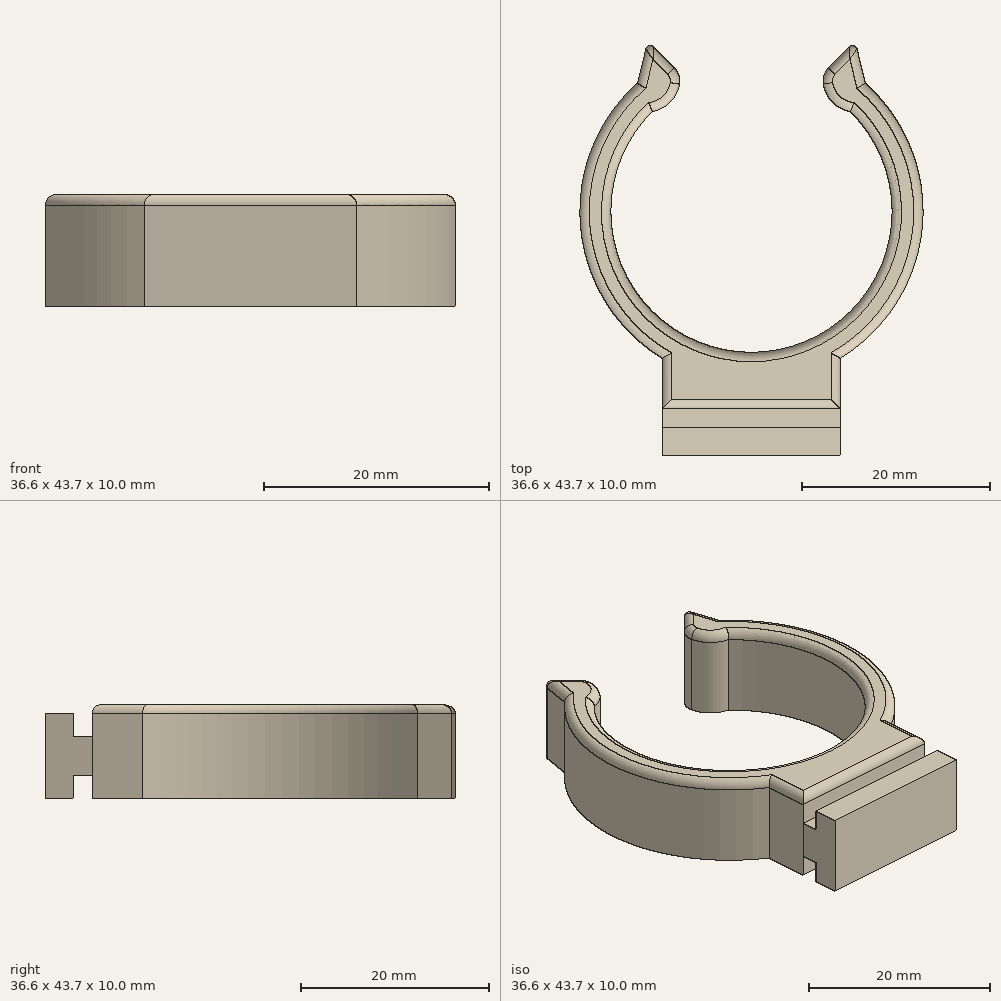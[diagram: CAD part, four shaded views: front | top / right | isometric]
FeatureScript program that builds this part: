
annotation { "Feature Type Name" : "Feature", "Feature Type Description" : "" }
export const myFeature = defineFeature(function(context is Context, id is Id, definition is map)
    precondition{}
    {
        {
            var Q0;
            Q0=qCreatedBy(makeId("Front.planeOp"),FACE);
            var sketch = newSketch(context, id + "F0", { "sketchPlane" : qUnion([Q0])});
            skLineSegment(sketch, "E0.bottom", {"start": v(-9.5, 5) * mm, "end": v(9.5, 5) * mm});
            skLineSegment(sketch, "E0.top", {"start": v(-9.5, -5) * mm, "end": v(9.5, -5) * mm});
            skLineSegment(sketch, "E0.left", {"start": v(-9.5, 5) * mm, "end": v(-9.5, -5) * mm});
            skLineSegment(sketch, "E0.right", {"start": v(9.5, 5) * mm, "end": v(9.5, -5) * mm});
            skLineSegment(sketch, "E1", {"start": v(-9.5, 5) * mm, "end": v(9.5, -5) * mm, "construction": true});
            skLineSegment(sketch, "E2", {"start": v(9.5, 5) * mm, "end": v(-9.5, -5) * mm, "construction": true});
            skSolve(sketch);
        }
        {
            var Q0;
            Q0 = qSketchRegion(id + "F0", true);
            extrude(context, id + "F1", {"entities" : qUnion([Q0]), "depth" : 6 * mm});
        }
        {
            var Q0;
            Q0=qCreatedBy(makeId("Top.planeOp"),FACE);
            var sketch = newSketch(context, id + "F2", { "sketchPlane" : qUnion([Q0])});
            skCircle(sketch, "E3", {"center": v(0, 15) * mm, "radius": 15 * mm});
            skCircle(sketch, "E4", {"center": v(0, 15) * mm, "radius": 18.3 * mm});
            skSolve(sketch);
        }
        {
            var Q0;
            Q0 = qSketchRegion(id + "F2", true);
            extrude(context, id + "F3", {"entities" : qUnion([Q0]), "operationType" : NewBodyOperationType.ADD, "endBound" : BoundingType.SYMMETRIC, "depth" : 10 * mm});
        }
        {
            var Q0;
            Q0=makeQuery(id+"F3.opExtrude","CAP_FACE",FACE,{"disambiguationData":[OSD([sQuery(id+"F2.wireOp",EDGE,"E3"),sQuery(id+"F2.wireOp",EDGE,"E4")])],"isStart":false});
            var sketch = newSketch(context, id + "F4", { "sketchPlane" : qUnion([Q0])});
            skCircle(sketch, "E5", {"center": v(0, 33.3) * mm, "radius": 13 * mm});
            skSolve(sketch);
        }
        {
            var Q0;
            Q0 = qSketchRegion(id + "F4", true);
            var Q1;
            Q1=makeQuery(id+"F3.opExtrude","CAP_FACE",FACE,{"disambiguationData":[OSD([sQuery(id+"F2.wireOp",EDGE,"E3"),sQuery(id+"F2.wireOp",EDGE,"E4")])],"isStart":true});
            extrude(context, id + "F5", {"entities" : qUnion([Q0]), "operationType" : NewBodyOperationType.REMOVE, "endBound" : BoundingType.UP_TO_SURFACE, "oppositeDirection" : true, "endBoundEntityFace" : qUnion([Q1]), "depth" : 25 * mm});
        }
        {
            var Q0;
            {var subQ0=sQuery(id+"F0.wireOp",EDGE,"E0.right");var subQ1=sQuery(id+"F2.wireOp",EDGE,"E3");var subQ2=sQuery(id+"F2.wireOp",EDGE,"E4");var subQ3=makeQuery(id+"F3.opExtrude","CAP_FACE",FACE,{"disambiguationData":[OSD([subQ1,subQ2])],"isStart":false});Q0=makeQuery(id+"F5.boolean.opBoolean","SPLIT",FACE,{"disambiguationData":[TD([makeQuery(id+"F1.opExtrude","SWEPT_FACE",FACE,{"disambiguationData":[OSD([subQ0])]})])],"derivedFrom":subQ3});}
            var sketch = newSketch(context, id + "F6", { "sketchPlane" : qUnion([Q0])});
            skArc(sketch, "E6", {"start": v(7.67, 29.76) * mm, "mid": v(8.25, 27.12) * mm, "end": v(10.53, 25.68) * mm});
            skLineSegment(sketch, "E7", {"start": v(7.67, 29.76) * mm, "end": v(11.04, 33.22) * mm});
            skLineSegment(sketch, "E8", {"start": v(11.04, 33.22) * mm, "end": v(12.15, 28.68) * mm});
            skArc(sketch, "E9", {"start": v(10.53, 25.68) * mm, "mid": v(11.92, 26.87) * mm, "end": v(12.15, 28.68) * mm});
            skLineSegment(sketch, "E10", {"start": v(0, 0) * mm, "end": v(0, 34.22) * mm, "construction": true});
            skArc(sketch, "E11.MirrorCS", {"start": v(-10.53, 25.68) * mm, "mid": v(-11.92, 26.87) * mm, "end": v(-12.15, 28.68) * mm});
            skArc(sketch, "E12.MirrorCS", {"start": v(-7.67, 29.76) * mm, "mid": v(-8.25, 27.12) * mm, "end": v(-10.53, 25.68) * mm});
            skLineSegment(sketch, "E13.MirrorCS", {"start": v(-11.04, 33.22) * mm, "end": v(-12.15, 28.68) * mm});
            skLineSegment(sketch, "E14.MirrorCS", {"start": v(-7.67, 29.76) * mm, "end": v(-11.04, 33.22) * mm});
            skSolve(sketch);
        }
        {
            var Q0;
            Q0 = qSketchRegion(id + "F6", true);
            var Q1;
            {var subQ0=sQuery(id+"F0.wireOp",EDGE,"E0.left");var subQ1=sQuery(id+"F2.wireOp",EDGE,"E4");var subQ2=sQuery(id+"F2.wireOp",EDGE,"E3");var subQ3=makeQuery(id+"F3.opExtrude","CAP_FACE",FACE,{"disambiguationData":[OSD([subQ2,subQ1])],"isStart":true});Q1=makeQuery(id+"F5.boolean.opBoolean","SPLIT",FACE,{"disambiguationData":[TD([makeQuery(id+"F1.opExtrude","SWEPT_FACE",FACE,{"disambiguationData":[OSD([subQ0])]})])],"derivedFrom":subQ3});}
            extrude(context, id + "F7", {"entities" : qUnion([Q0]), "operationType" : NewBodyOperationType.ADD, "endBound" : BoundingType.UP_TO_SURFACE, "oppositeDirection" : true, "endBoundEntityFace" : qUnion([Q1]), "depth" : 25 * mm});
        }
        {
            var Q0;
            Q0=makeQuery(id+"F7.opExtrude","SWEPT_EDGE",EDGE,{"disambiguationData":[OSD([sQuery(id+"F6.wireOp",EDGE,"E12.MirrorCS"),sQuery(id+"F6.wireOp",EDGE,"E14.MirrorCS")])]});
            var Q1;
            Q1=makeQuery(id+"F7.opExtrude","SWEPT_EDGE",EDGE,{"disambiguationData":[OSD([sQuery(id+"F6.wireOp",EDGE,"E6"),sQuery(id+"F6.wireOp",EDGE,"E7")])]});
            fillet(context, id + "F8", {"entities" : qUnion([Q0, Q1]), "radius" : 2 * mm, "tangentPropagation" : true, "allowEdgeOverflow" : false});
        }
        {
            var Q0;
            Q0=makeQuery(id+"F7.opExtrude","SWEPT_EDGE",EDGE,{"disambiguationData":[OSD([sQuery(id+"F6.wireOp",EDGE,"E13.MirrorCS"),sQuery(id+"F6.wireOp",EDGE,"E14.MirrorCS")])]});
            var Q1;
            Q1=makeQuery(id+"F7.opExtrude","SWEPT_EDGE",EDGE,{"disambiguationData":[OSD([sQuery(id+"F6.wireOp",EDGE,"E7"),sQuery(id+"F6.wireOp",EDGE,"E8")])]});
            fillet(context, id + "F9", {"entities" : qUnion([Q0, Q1]), "radius" : .5 * mm, "tangentPropagation" : true, "allowEdgeOverflow" : false});
        }
        {
            var Q0;
            Q0=makeQuery(id+"F1.opExtrude","SWEPT_FACE",FACE,{"disambiguationData":[OSD([sQuery(id+"F0.wireOp",EDGE,"E0.left")])]});
            var sketch = newSketch(context, id + "F10", { "sketchPlane" : qUnion([Q0])});
            skLineSegment(sketch, "E15.bottom", {"start": v(8, 4) * mm, "end": v(11, 4) * mm});
            skLineSegment(sketch, "E15.top", {"start": v(8, -5) * mm, "end": v(11, -5) * mm});
            skLineSegment(sketch, "E15.right", {"start": v(11, 4) * mm, "end": v(11, -5) * mm});
            skLineSegment(sketch, "E16", {"start": v(6, 1.6) * mm, "end": v(6, -2.6) * mm});
            skLineSegment(sketch, "E17", {"start": v(8, 4) * mm, "end": v(8, 1.6) * mm});
            skLineSegment(sketch, "E18", {"start": v(8, -5) * mm, "end": v(8, -2.6) * mm});
            skLineSegment(sketch, "E19", {"start": v(6, 1.6) * mm, "end": v(8, 1.6) * mm});
            skLineSegment(sketch, "E20", {"start": v(6, -2.6) * mm, "end": v(8, -2.6) * mm});
            skSolve(sketch);
        }
        {
            var Q0;
            Q0=makeQuery(id+"F10.imprint","IMPRINT",FACE,{"disambiguationData":[TD([[makeQuery(id+"F10.imprint","IMPRINT",EDGE,{"derivedFrom":sQuery(id+"F10.wireOp",EDGE,"E15.bottom")}),-1.0]])]});
            var Q1;
            Q1=makeQuery(id+"F1.opExtrude","SWEPT_FACE",FACE,{"disambiguationData":[OSD([sQuery(id+"F0.wireOp",EDGE,"E0.right")])]});
            extrude(context, id + "F11", {"entities" : qUnion([Q0]), "endBound" : BoundingType.UP_TO_SURFACE, "oppositeDirection" : true, "endBoundEntityFace" : qUnion([Q1]), "depth" : 25 * mm});
        }
        {
            var Q0;
            Q0=makeQuery(id+"F7.boolean.opBoolean","MERGE",FACE,{"derivedFrom":[makeQuery(id+"F3.boolean.opBoolean","MERGE",FACE,{"derivedFrom":[makeQuery(id+"F1.opExtrude","SWEPT_FACE",FACE,{"disambiguationData":[OSD([sQuery(id+"F0.wireOp",EDGE,"E0.bottom")])]}),makeQuery(id+"F3.opExtrude","CAP_FACE",FACE,{"disambiguationData":[OSD([sQuery(id+"F2.wireOp",EDGE,"E3"),sQuery(id+"F2.wireOp",EDGE,"E4")])],"isStart":false})]}),makeQuery(id+"F7.opExtrude","CAP_FACE",FACE,{"disambiguationData":[OSD([sQuery(id+"F6.wireOp",EDGE,"E6"),sQuery(id+"F6.wireOp",EDGE,"E7"),sQuery(id+"F6.wireOp",EDGE,"E8"),sQuery(id+"F6.wireOp",EDGE,"E9")])],"isStart":true}),makeQuery(id+"F7.opExtrude","CAP_FACE",FACE,{"disambiguationData":[OSD([sQuery(id+"F6.wireOp",EDGE,"E11.MirrorCS"),sQuery(id+"F6.wireOp",EDGE,"E12.MirrorCS"),sQuery(id+"F6.wireOp",EDGE,"E13.MirrorCS"),sQuery(id+"F6.wireOp",EDGE,"E14.MirrorCS")])],"isStart":true})]});
            fillet(context, id + "F12", {"entities" : qUnion([Q0]), "radius" : 1 * mm, "tangentPropagation" : true, "allowEdgeOverflow" : false});
        }
    });
